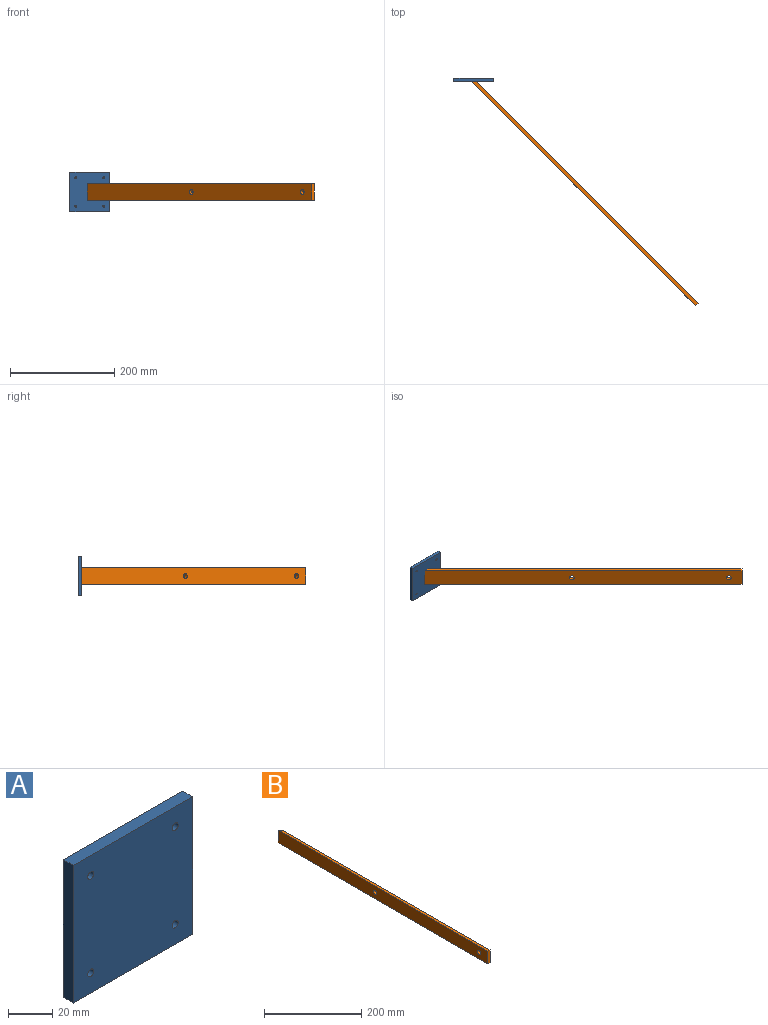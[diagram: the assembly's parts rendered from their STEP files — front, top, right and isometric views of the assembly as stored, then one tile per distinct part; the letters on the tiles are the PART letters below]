
ASSEMBLY  parts=2 mates=1
PART A: 10 faces, bbox 76.2x6.4x76.2 mm
  f0: plane 76.2x6.35mm, normal (0,0,1), area 483.9mm2, adj f1,f4,f8,f9
  f1: plane 76.2x6.35mm, normal (-1,0,0), area 483.9mm2, adj f0,f2,f8,f9
  f2: plane 76.2x6.35mm, normal (0,0,-1), area 483.9mm2, adj f1,f4,f8,f9
  f3: cylinder r=1.98mm len=6.35mm, axis (0,1,0), area 79mm2, adj f8,f9
  f4: plane 76.2x6.35mm, normal (1,0,0), area 483.9mm2, adj f0,f2,f8,f9
  f5: cylinder r=1.98mm len=6.35mm, axis (0,1,0), area 79mm2, adj f8,f9
  f6: cylinder r=1.98mm len=6.35mm, axis (0,1,0), area 79mm2, adj f8,f9
  f7: cylinder r=1.98mm len=6.35mm, axis (0,1,0), area 79mm2, adj f8,f9
  f8: plane 76.2x76.2mm, normal (0,-1,0), area 5757.1mm2, adj f0,f1,f2,f3,f4,f5,f6,f7
  f9: plane 76.2x76.2mm, normal (0,1,0), area 5757.1mm2, adj f0,f1,f2,f3,f4,f5,f6,f7
PART B: 8 faces, bbox 6.4x609.6x31.8 mm
  f0: plane 603.25x31.75mm, normal (1,0,0), area 19010.7mm2, adj f1,f2,f3,f4,f5,f7
  f1: plane 609.6x6.35mm, normal (0,0,1), area 3850.8mm2, adj f0,f2,f6,f7
  f2: plane 31.75x6.35mm, normal (0,-1,0), area 201.6mm2, adj f0,f1,f3,f6
  f3: plane 609.6x6.35mm, normal (0,0,-1), area 3850.8mm2, adj f0,f2,f6,f7
  f4: cylinder r=4.76mm len=9.53mm, axis (-1,0,0), area 190mm2, adj f0,f6
  f5: cylinder r=4.76mm len=9.53mm, axis (-1,0,0), area 190mm2, adj f0,f6
  f6: plane 609.6x31.75mm, normal (-1,0,0), area 19212.3mm2, adj f1,f2,f3,f4,f5,f7
  f7: plane 31.75x6.35mm, normal (0.71,0.71,0), area 285.1mm2, adj f0,f1,f3,f6
PLACE A at identity
PLACE B rot(axis=(0,0,1),45deg) t=(232.73,-243.57,0)mm
MATE fastened B.f7 <-> A.f8  axis (0,1,0) through (0,-6.35,0)mm
